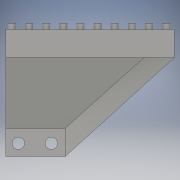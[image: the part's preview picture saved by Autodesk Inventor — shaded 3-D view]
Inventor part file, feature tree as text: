
AUTODESK INVENTOR PART (.ipt)
format: ipt  version: 2016 (Build 200138000, 138)  size: 685,056 bytes
history: native  units: in
note: dims shown in document units (in); Inventor stores cm internally (conversion verified against a paired STEP export)
features: sketch x11, loft x4, other x4, extrude x3, sweep x1, hole x1
ambient origin geometry x8: Origin, YZ Plane, XZ Plane, XY Plane, X Axis, Y Axis, Z Axis, Center Point
bodies: Solid1 (feature_tree)
feature tree (24):
  extrude  "Extrusion1"  Depth=0.5in
  extrude  "Extrusion2"  Depth=0.5in TaperAngle=0.0deg
  sketch  "Sketch4"  dims[d22=0.75in d23=0.0in d25=0.0125in]
  sketch  "Sketch6"  dims[d41=1.0in d55=0.0in d56=0.0in]
  sweep  "Sweep4"
  sketch  "Sketch10"  dims[d57=0.0in d58=90.0deg d59=0.0in d60=90.0deg]
  sketch  "Sketch11"  dims[d61=0.0in d62=90.0deg d63=0.0in d64=90.0deg]
  loft  "Loft2"
  loft  "Loft3"
  sketch  "Sketch12"  dims[d65=0.0in d66=90.0deg d67=0.0in d68=90.0deg]
  sketch  "Sketch13"  dims[d69=0.0in d70=90.0deg d71=0.0in d72=90.0deg]
  sketch  "Sketch14"  dims[d74=0.1575in d75=0.75in d76=0.2362in d77=0.1181in d78=0.5635in d79=1.0in d80=0.8108in d81=3.937in d83=0.2165in d84=1.9685in d86=0.2087in]
  loft  "Loft4"
  loft  "Loft5"
  hole  "Hole5"  [1 undecoded]
  extrude  "Extrusion5"  Depth=3.937in
  sketch  "Sketch1"  dims[d0=0.75in d1=0.5in]
  sketch  "Sketch3"  dims[d2=0.4173in d3=0.5in d4=0.0in]
  other  "Edges3"
  other  "Edges4"
  other  "Edges5"
  other  "Edges6"
  sketch  "Sketch15"  dims[d89=0.0787in d90=0.0in]
  sketch  "Sketch16"  dims[d5=1.0in d6=1.0in]
note: 1 required parameter value undecoded (feature->parameter linkage not recoverable at this tier; creation-order binding heuristic only, values carry confidence <= 0.55)
